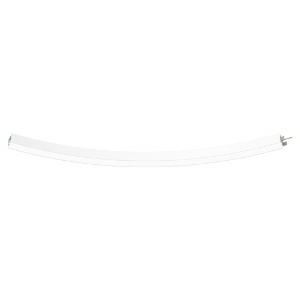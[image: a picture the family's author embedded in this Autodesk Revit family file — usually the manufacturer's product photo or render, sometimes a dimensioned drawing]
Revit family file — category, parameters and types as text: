
# Revit family: super-g_slim_super_g_slim_dir_ind_5200_45deg_hl_ps_led_66w__10560lm__3000k__cri80_430-3860_a879
name_source: partatom
category: Leuchten
revit_build: Autodesk Revit 2016 (Build: 20190508_0715(x64)
units: mm (PartAtom-declared; Revit-internal decimal feet)

## family parameters
Basisbauteil = Fläche
Beim Laden mit Abzugskörper schneiden = Nein
Bemaßung runder Anschluss = Durchmesser verwenden
Gemeinsam genutzt = Nein
Lichtquelle = Nein
Raumberechnungspunkt = Nein
Teiletyp = Normal

## types (1)
- 430-3860-D01 (1 x LED, 754.3 lm, 3000K)
    Beschreibung = The insert consists of aluminum-extruded profile. Charming SOFT-EDGE design ensure unparalleled styling. The ballast is integrated and allows for an operation with 220-240V (50/60Hz). SUPER-G SLIM (# 430-3860) ist not dimmable (on/off).
    CIE Flux Codes = 48 79 96 66 85
    Color Rendering = 1B/80…89
    Color Temperature = 3000K
    Height = 90 mm
    Hersteller = Prolicht
    Lamp Light Flux = 754.3 lm
    Lamp count = 1
    Lampe = 1 x LED
    Length = 146 mm
    Luminous efficacy = 123 lm/W
    ModVariant = Nein
    Modell = 430-3860
    Mounting Place = Ceiling
    Mounting Type = Pendant
    Number of Poles = 1
    OnlyDefault = Ja
    Power Factor = 1
    Product Name = SUPER-G SLIM__SUPER G SLIM DIR/IND 5200/45° HL PS LED 66W  10560lm  3000K  CRI80
    Product group = Suspended profile systems
    ProductGroupID = 944
    Protection Class = Protection class
    Protection Degree = Degree of protection
    RLX_Detail_Level = 1
    RlxData = <blob elided: 28725 chars, md5=273f38e7>
    Scheinlast = 73 VA
    Socket = socket
    Standby Power = 0 W
    System Light Flux = 8934 lm
    System Power = 73 W
    Typenbild = 430-3860.jpg
    URL = http://relux.com
    VarID = 430-3860-d01
    Voltage = 0 V
    Vorgabe-Ansicht = 1800 mm
    Weight = 0.00 kg
    Width = 65 mm

## geometry (parser evidence)
native form markers: Blend x4, Sweep x69
no freeform markers — native parametric forms only
